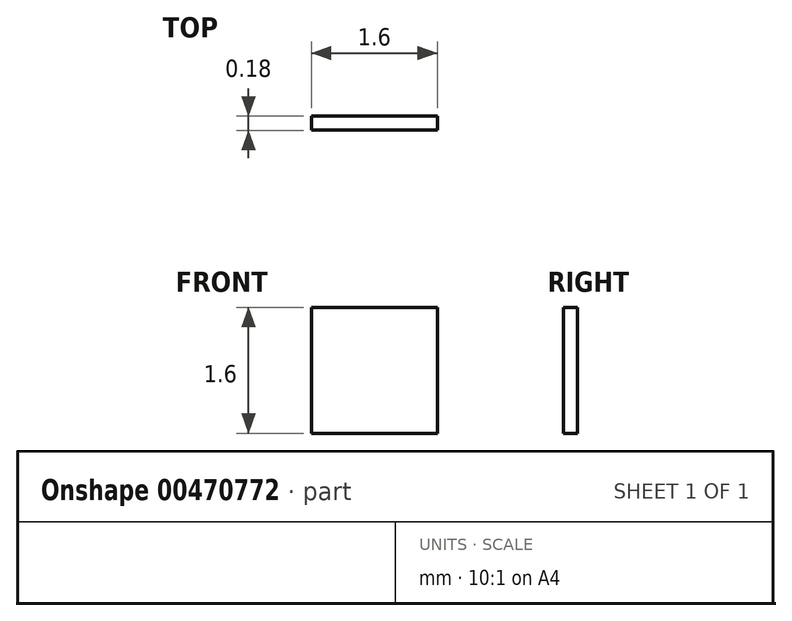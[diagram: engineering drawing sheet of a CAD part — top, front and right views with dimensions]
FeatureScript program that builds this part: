
annotation { "Feature Type Name" : "Feature", "Feature Type Description" : "" }
export const myFeature = defineFeature(function(context is Context, id is Id, definition is map)
    precondition{}
    {
        {
            var Q0;
            Q0=qCreatedBy(makeId("Front.planeOp"),FACE);
            var sketch = newSketch(context, id + "F0", { "sketchPlane" : qUnion([Q0])});
            skLineSegment(sketch, "E0.bottom", {"start": v(0.8, -0.8) * mm, "end": v(-0.8, -0.8) * mm});
            skLineSegment(sketch, "E0.top", {"start": v(0.8, 0.8) * mm, "end": v(-0.8, 0.8) * mm});
            skLineSegment(sketch, "E0.left", {"start": v(0.8, -0.8) * mm, "end": v(0.8, 0.8) * mm});
            skLineSegment(sketch, "E0.right", {"start": v(-0.8, -0.8) * mm, "end": v(-0.8, 0.8) * mm});
            skPoint(sketch, "E0.middle", {"position": v(0, 0) * mm});
            skSolve(sketch);
        }
        {
            var Q0;
            Q0 = qSketchRegion(id + "F0", true);
            extrude(context, id + "F1", {"entities" : qUnion([Q0]), "depth" : 0.18 * mm});
        }
    });
